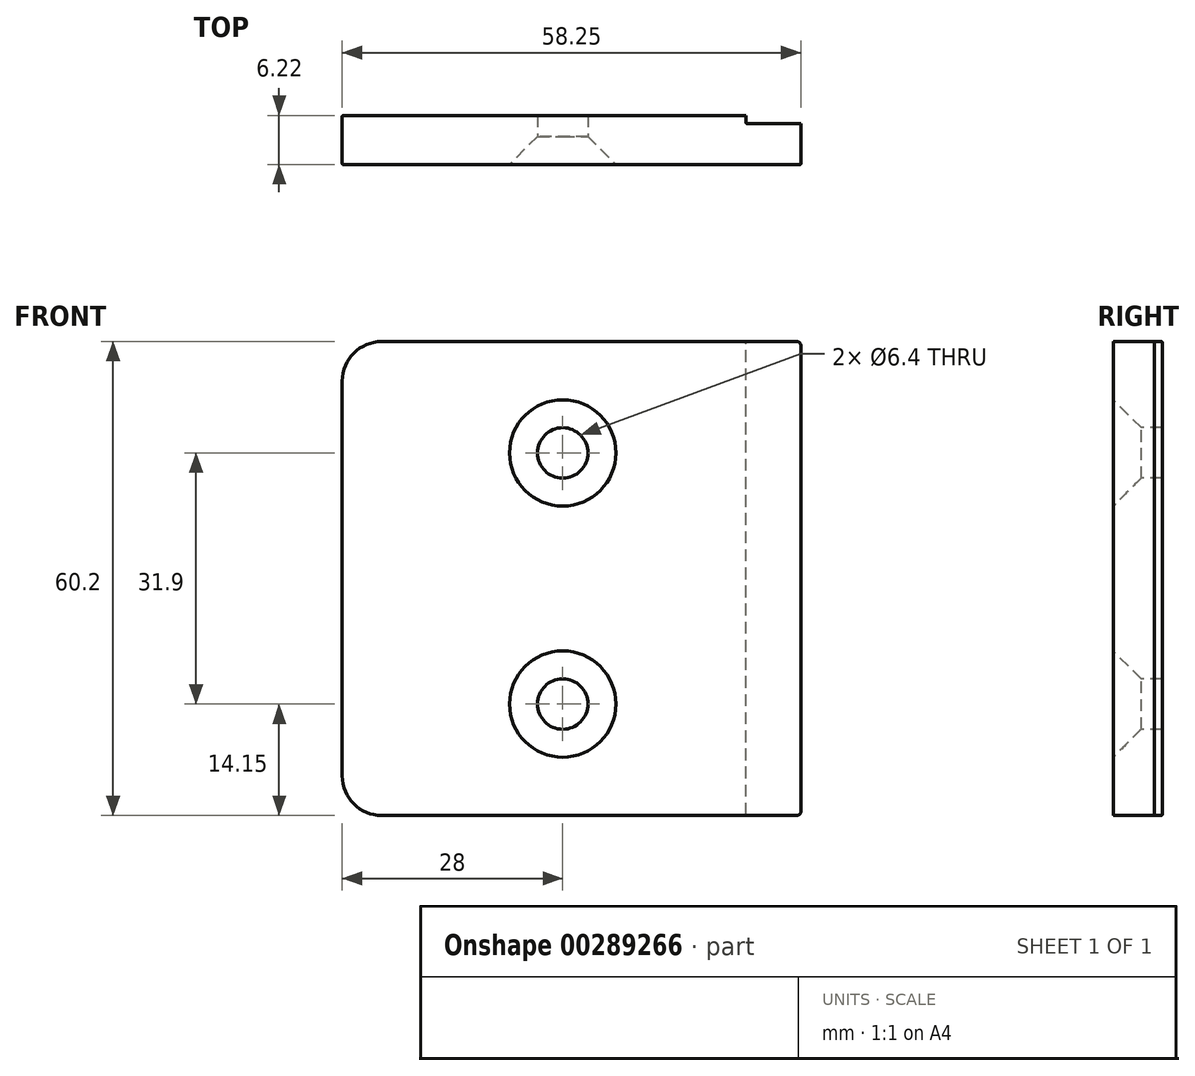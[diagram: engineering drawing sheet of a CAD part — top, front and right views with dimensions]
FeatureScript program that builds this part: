
annotation { "Feature Type Name" : "Feature", "Feature Type Description" : "" }
export const myFeature = defineFeature(function(context is Context, id is Id, definition is map)
    precondition{}
    {
        {
            var Q0;
            Q0=qCreatedBy(makeId("Front.planeOp"),FACE);
            var sketch = newSketch(context, id + "F0", { "sketchPlane" : qUnion([Q0])});
            skLineSegment(sketch, "E0.bottom", {"start": v(-0.5, 0) * mm, "end": v(-53.25, 0) * mm});
            skLineSegment(sketch, "E0.top", {"start": v(-0.5, 60.2) * mm, "end": v(-53.25, 60.2) * mm});
            skLineSegment(sketch, "E0.left", {"start": v(0, 0.5) * mm, "end": v(0, 59.7) * mm});
            skLineSegment(sketch, "E0.right", {"start": v(-58.25, 5) * mm, "end": v(-58.25, 55.2) * mm});
            skPoint(sketch, "E1.visualSharp", {"position": v(-58.25, 60.2) * mm});
            skArc(sketch, "E1.filletArc", {"start": v(-53.25, 60.2) * mm, "mid": v(-56.79, 58.74) * mm, "end": v(-58.25, 55.2) * mm});
            skPoint(sketch, "E2.visualSharp", {"position": v(-58.25, 0) * mm});
            skArc(sketch, "E2.filletArc", {"start": v(-58.25, 5) * mm, "mid": v(-56.79, 1.46) * mm, "end": v(-53.25, 0) * mm});
            skPoint(sketch, "E3.visualSharp", {"position": v(0, 0) * mm});
            skArc(sketch, "E3.filletArc", {"start": v(-0.5, 0) * mm, "mid": v(-0.15, 0.15) * mm, "end": v(0, 0.5) * mm});
            skPoint(sketch, "E4.visualSharp", {"position": v(0, 60.2) * mm});
            skArc(sketch, "E4.filletArc", {"start": v(0, 59.7) * mm, "mid": v(-0.15, 60.05) * mm, "end": v(-0.5, 60.2) * mm});
            skSolve(sketch);
        }
        {
            var Q0;
            Q0=makeQuery(id+"F0.imprint","IMPRINT",FACE,{"disambiguationData":[TD([[makeQuery(id+"F0.imprint","IMPRINT",EDGE,{"derivedFrom":sQuery(id+"F0.wireOp",EDGE,"E0.bottom")}),-1.0]])]});
            extrude(context, id + "F1", {"entities" : qUnion([Q0]), "depth" : 6.22 * mm});
        }
        {
            var Q0;
            Q0=makeQuery(id+"F1.opExtrude","SWEPT_FACE",FACE,{"disambiguationData":[OSD([sQuery(id+"F0.wireOp",EDGE,"E0.top")])]});
            var sketch = newSketch(context, id + "F2", { "sketchPlane" : qUnion([Q0])});
            skLineSegment(sketch, "E5.bottom", {"start": v(0, 0) * mm, "end": v(-7, 0) * mm});
            skLineSegment(sketch, "E5.top", {"start": v(0, -1) * mm, "end": v(-7, -1) * mm});
            skLineSegment(sketch, "E5.left", {"start": v(0, 0) * mm, "end": v(0, -1) * mm});
            skLineSegment(sketch, "E5.right", {"start": v(-7, 0) * mm, "end": v(-7, -1) * mm});
            skSolve(sketch);
        }
        {
            var Q0;
            Q0 = qSketchRegion(id + "F2", true);
            extrude(context, id + "F3", {"entities" : qUnion([Q0]), "operationType" : NewBodyOperationType.REMOVE, "endBound" : BoundingType.THROUGH_ALL, "oppositeDirection" : true, "depth" : 25 * mm});
        }
        {
            var Q0;
            Q0=makeQuery(id+"F1.opExtrude","CAP_EDGE",EDGE,{"disambiguationData":[OSD([sQuery(id+"F0.wireOp",EDGE,"E0.top")])],"isStart":false});
            var Q1;
            Q1=makeQuery(id+"F1.opExtrude","CAP_EDGE",EDGE,{"disambiguationData":[OSD([sQuery(id+"F0.wireOp",EDGE,"E0.top")])],"isStart":true});
            var Q2;
            Q2=makeQuery(id+"F3.boolean.opBoolean","COPY",EDGE,{"derivedFrom":makeQuery(id+"F3.opExtrude","SWEPT_EDGE",EDGE,{"disambiguationData":[OSD([sQuery(id+"F0.wireOp",EDGE,"E0.top"),sQuery(id+"F2.wireOp",EDGE,"E5.bottom"),sQuery(id+"F2.wireOp",EDGE,"E5.right")])]})});
            var Q3;
            Q3=makeQuery(id+"F3.boolean.opBoolean","COPY",EDGE,{"derivedFrom":makeQuery(id+"F3.opExtrude","CAP_EDGE",EDGE,{"disambiguationData":[OSD([sQuery(id+"F2.wireOp",EDGE,"E5.top")])],"isStart":true})});
            var Q4;
            Q4=makeQuery(id+"F3.boolean.opBoolean","COPY",EDGE,{"derivedFrom":makeQuery(id+"F3.opExtrude","CAP_EDGE",EDGE,{"disambiguationData":[OSD([sQuery(id+"F2.wireOp",EDGE,"E5.right")])],"isStart":true})});
            var Q5;
            Q5=makeQuery(id+"F3.boolean.opBoolean","INTERSECT",EDGE,{"derivedFrom":[makeQuery(id+"F1.opExtrude","SWEPT_FACE",FACE,{"disambiguationData":[OSD([sQuery(id+"F0.wireOp",EDGE,"E0.bottom")])]}),makeQuery(id+"F3.opExtrude","SWEPT_FACE",FACE,{"disambiguationData":[OSD([sQuery(id+"F2.wireOp",EDGE,"E5.right")])]})]});
            var Q6;
            Q6=makeQuery(id+"F3.boolean.opBoolean","COPY",EDGE,{"derivedFrom":makeQuery(id+"F3.opExtrude","SWEPT_EDGE",EDGE,{"disambiguationData":[OSD([sQuery(id+"F2.wireOp",EDGE,"E5.top"),sQuery(id+"F2.wireOp",EDGE,"E5.right")])]})});
            fillet(context, id + "F4", {"entities" : qUnion([Q0, Q1, Q2, Q3, Q4, Q5, Q6]), "radius" : 0.1 * mm, "tangentPropagation" : true, "allowEdgeOverflow" : false});
        }
        {
            var Q0;
            Q0=makeQuery(id+"F1.opExtrude","CAP_FACE",FACE,{"disambiguationData":[OSD([sQuery(id+"F0.wireOp",EDGE,"E0.bottom"),sQuery(id+"F0.wireOp",EDGE,"E0.top"),sQuery(id+"F0.wireOp",EDGE,"E0.left"),sQuery(id+"F0.wireOp",EDGE,"E0.right"),sQuery(id+"F0.wireOp",EDGE,"E1.filletArc"),sQuery(id+"F0.wireOp",EDGE,"E2.filletArc"),sQuery(id+"F0.wireOp",EDGE,"E3.filletArc"),sQuery(id+"F0.wireOp",EDGE,"E4.filletArc")])],"isStart":false});
            var sketch = newSketch(context, id + "F5", { "sketchPlane" : qUnion([Q0])});
            skCircle(sketch, "E6", {"center": v(-30.25, 46.05) * mm, "radius": 3 * mm});
            skCircle(sketch, "E7.MirrorC", {"center": v(-30.25, 14.15) * mm, "radius": 3 * mm});
            skSolve(sketch);
        }
        {
            var Q0;
            Q0=sQuery(id+"F5.wireOp",VERTEX,"E6.center");
            var Q1;
            Q1=sQuery(id+"F5.wireOp",VERTEX,"E7.MirrorC.center");
            var Q2;
            Q2=makeQuery(id+"F1.opExtrude","SWEPT_BODY",BODY,{"disambiguationData":[OSD([sQuery(id+"F0.wireOp",EDGE,"E0.bottom"),sQuery(id+"F0.wireOp",EDGE,"E0.top"),sQuery(id+"F0.wireOp",EDGE,"E0.left"),sQuery(id+"F0.wireOp",EDGE,"E0.right"),sQuery(id+"F0.wireOp",EDGE,"E1.filletArc"),sQuery(id+"F0.wireOp",EDGE,"E2.filletArc"),sQuery(id+"F0.wireOp",EDGE,"E3.filletArc"),sQuery(id+"F0.wireOp",EDGE,"E4.filletArc")])]});
            hole(context, id + "F6", {"style" : HoleStyle.C_SINK, "endStyle" : HoleEndStyle.THROUGH, "holeDiameter" : 6.4 * mm, "cSinkDiameter" : 13.5 * mm, "cSinkAngle" : 90 * degree, "tappedDepth" : 10 * mm, "tapClearance" : 3, "locations" : qUnion([Q0, Q1]), "scope" : qUnion([Q2])});
        }
    });
